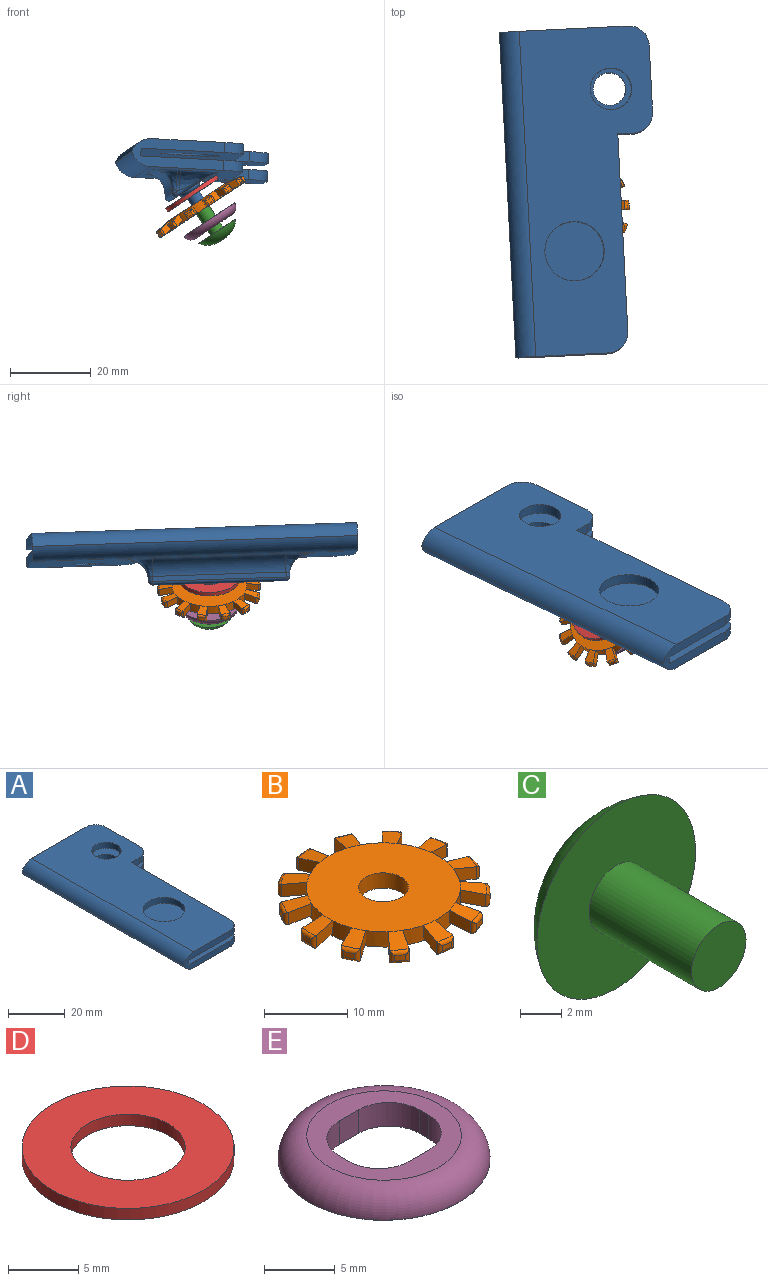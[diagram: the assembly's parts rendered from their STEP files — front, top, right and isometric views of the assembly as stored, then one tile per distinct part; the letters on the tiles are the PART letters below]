
ASSEMBLY  parts=5 mates=4
PART A: 50 faces, bbox 37.3x81.2x19.6 mm
  f0: plane 81.23x32.57mm, normal (0,0,-1), area 1317mm2, adj f1,f2,f3,f4,f5,f13,f14,f15
  f1: plane 31.76x6.93mm, normal (0,1,0), area 154.3mm2, adj f0,f9,f10,f11,f12,f13,f18,f19
  f2: plane 16.6x2.5mm, normal (1,0,0), area 41.5mm2, adj f0,f12,f13,f14
  f3: plane 3.89x2.5mm, normal (0,-1,0), area 9.7mm2, adj f0,f4,f12,f14
  f4: plane 49.06x2.5mm, normal (1,0,0), area 122.7mm2, adj f0,f3,f12,f15
  f5: plane 22.87x6.93mm, normal (0,-1,0), area 109.9mm2, adj f0,f9,f10,f11,f12,f15,f16,f19
  f6: plane 49.06x2.5mm, normal (1,0,0), area 122.7mm2, adj f7,f9,f11,f16
  f7: plane 3.89x2.5mm, normal (0,-1,0), area 9.7mm2, adj f6,f9,f11,f17
  f8: plane 16.6x2.5mm, normal (1,0,0), area 41.5mm2, adj f9,f11,f17,f18
  f9: plane 80.66x32mm, normal (0,0,1), area 1830.9mm2, adj f1,f5,f6,f7,f8,f16,f17,f18
  f10: plane 80.66x1.93mm, normal (1,0,0), area 155.7mm2, adj f1,f5,f11,f12
  f11: plane 80.66x34.5mm, normal (0,0,-1), area 2032.6mm2, adj f1,f5,f6,f7,f8,f10,f16,f17
  f12: plane 80.66x34.5mm, normal (0,0,1), area 2234.7mm2, adj f1,f2,f3,f4,f5,f10,f13,f14
  f13: cylinder r=5mm len=5mm, axis (0,0,-1), area 19.6mm2, adj f0,f1,f2,f12
  f14: cylinder r=5mm len=5mm, axis (0,0,-1), area 19.6mm2, adj f0,f2,f3,f12
  f15: cylinder r=5mm len=5mm, axis (0,0,-1), area 19.6mm2, adj f0,f4,f5,f12
  f16: cylinder r=5mm len=5mm, axis (0,0,-1), area 19.6mm2, adj f5,f6,f9,f11
  f17: cylinder r=5mm len=5mm, axis (0,0,-1), area 19.6mm2, adj f7,f8,f9,f11
  f18: cylinder r=5mm len=5mm, axis (0,0,-1), area 19.6mm2, adj f1,f8,f9,f11
  f19: cylinder r=5mm len=80.66mm, axis (0,1,0), area 507.7mm2, adj f1,f5,f9,f20
  f20: cylinder r=5mm len=80.66mm, axis (0,-1,0), area 507.7mm2, adj f0,f1,f5,f19
  f21: cylinder r=5.15mm len=10.3mm, axis (0,0,1), area 80.9mm2, adj f9,f11
  f22: cylinder r=4.04mm len=8.09mm, axis (0,0,-1), area 63.5mm2, adj f0,f12
  f23: cylinder r=7.36mm len=14.72mm, axis (0,0,1), area 115.6mm2, adj f9,f11
  f24: plane 33.07x7.22mm, normal (0.59,0,-0.81), area 269.9mm2, adj f28,f31,f34,f35,f43
  f25: plane 33.07x1.24mm, normal (-0.99,0,-0.12), area 41.2mm2, adj f29,f30,f34,f42
  f26: plane 0.75x0.51mm, normal (0,1,0), area 0.2mm2, adj f28,f29,f38
  f27: plane 0.75x0.51mm, normal (0,-1,0), area 0.2mm2, adj f30,f31,f39
  f28: cylinder r=0.97mm len=7.79mm, axis (-0.81,0,-0.59), area 9.1mm2, adj f24,f26,f32,f36
  f29: cylinder r=0.97mm len=1.35mm, axis (-0.12,0,0.99), area 1.3mm2, adj f25,f26,f32,f40
  f30: cylinder r=0.97mm len=1.35mm, axis (0.12,0,-0.99), area 1.3mm2, adj f25,f27,f33,f41
  f31: cylinder r=0.97mm len=7.79mm, axis (0.81,0,0.59), area 9.1mm2, adj f24,f27,f33,f37
  f32: sphere r=0.97mm, area 2.2mm2, adj f28,f29,f34
  f33: sphere r=0.97mm, area 2mm2, adj f30,f31,f34
  f34: cylinder r=0.97mm len=33.07mm, axis (0,-1,0), area 66.5mm2, adj f24,f25,f32,f33
  f35: cylinder r=5mm len=33.07mm, axis (0,1,0), area 104.9mm2, adj f0,f24,f36,f37
  f36: bspline ~10.06x5.97mm, area 51.8mm2, adj f0,f28,f35,f38
  f37: bspline ~10.06x5.97mm, area 51.8mm2, adj f0,f31,f35,f39
  f38: cylinder r=5mm len=5mm, axis (1,0,0), area 5.9mm2, adj f0,f26,f36,f40
  f39: cylinder r=5mm len=5mm, axis (-1,0,0), area 5.9mm2, adj f0,f27,f37,f41
  f40: bspline ~7.06x5.97mm, area 34mm2, adj f0,f29,f38,f42
  f41: bspline ~7.06x7mm, area 34mm2, adj f0,f30,f39,f42
  f42: cylinder r=5mm len=33.07mm, axis (0,1,0), area 239.5mm2, adj f0,f25,f40,f41
  f43: cylinder r=2.9mm len=5.8mm, axis (-0.59,0,0.81), area 0.3mm2, adj f24,f47
  f44: plane 4.01x3.23mm, normal (0.59,0,-0.81), area 3mm2, adj f45,f47
  f45: cylinder r=1.75mm len=8.71mm, axis (-0.59,0,0.81), area 90.6mm2, adj f44,f46
  f46: plane 3.5x2.82mm, normal (0.59,0,-0.81), area 5.3mm2, adj f45,f48
  f47: torus R=2.01mm, axis (0.59,0,-0.81), area 22.7mm2, adj f43,f44
  f48: cylinder r=1.18mm len=8.48mm, axis (0.59,0,-0.81), area 65mm2, adj f46,f49
  f49: plane 2.35x1.89mm, normal (0.59,0,-0.81), area 4.3mm2, adj f48
PART B: 121 faces, bbox 25.6x25.7x2.3 mm
  f0: cylinder r=9.24mm len=18.48mm, axis (0,0,-1), area 89.1mm2, adj f2,f3,f5,f7,f8,f14,f16,f17
  f1: cylinder r=3mm len=6mm, axis (0,0,-1), area 42.4mm2, adj f2,f3
  f2: plane 18.48x18.48mm, normal (0,0,1), area 239.9mm2, adj f0,f1,f4,f13,f22,f31,f40,f49
  f3: plane 18.48x18.48mm, normal (0,0,-1), area 239.9mm2, adj f0,f1
  f4: cone r=9.24mm half-angle=80deg, axis (0,0,-1), area 6.6mm2, adj f2,f7,f8,f9,f10,f11
  f5: cone r=12.79mm half-angle=80deg, axis (0,0,-1), area 6.2mm2, adj f0,f7,f8,f12
  f6: cylinder r=12.79mm len=1.39mm, axis (0,0,-1), area 1.1mm2, adj f9,f10,f11,f12
  f7: plane 2.98x2.33mm, normal (-0.98,-0.19,0), area 5.5mm2, adj f0,f4,f5,f10,f12
  f8: plane 3.03x2.33mm, normal (1,0,0), area 5.5mm2, adj f0,f4,f5,f11,f12
  f9: torus R=12.28mm, axis (0,0,1), area 1.4mm2, adj f4,f6,f10,f11
  f10: cylinder r=0.51mm len=1.79mm, axis (0,0,-1), area 1.2mm2, adj f4,f6,f7,f9,f12
  f11: cylinder r=0.51mm len=1.79mm, axis (0,0,-1), area 1.2mm2, adj f4,f6,f8,f9,f12
  f12: torus R=12.28mm, axis (0,0,1), area 1.8mm2, adj f5,f6,f7,f8,f10,f11
  f13: cone r=9.24mm half-angle=80deg, axis (0,0,-1), area 6.6mm2, adj f2,f16,f17,f18,f19,f20
  f14: cone r=12.79mm half-angle=80deg, axis (0,0,-1), area 6.2mm2, adj f0,f16,f17,f21
  f15: cylinder r=12.79mm len=1.17mm, axis (0,0,-1), area 1.1mm2, adj f18,f19,f20,f21
  f16: plane 2.37x2.33mm, normal (-0.78,-0.63,0), area 5.5mm2, adj f0,f13,f14,f19,f21
  f17: plane 2.69x2.33mm, normal (0.89,0.46,0), area 5.5mm2, adj f0,f13,f14,f20,f21
  f18: torus R=12.28mm, axis (0,0,1), area 1.4mm2, adj f13,f15,f19,f20
  f19: cylinder r=0.51mm len=1.79mm, axis (0,0,-1), area 1.2mm2, adj f13,f15,f16,f18,f21
  f20: cylinder r=0.51mm len=1.79mm, axis (0,0,-1), area 1.2mm2, adj f13,f15,f17,f18,f21
  f21: torus R=12.28mm, axis (0,0,1), area 1.8mm2, adj f14,f15,f16,f17,f19,f20
  f22: cone r=9.24mm half-angle=80deg, axis (0,0,-1), area 6.6mm2, adj f2,f25,f26,f27,f28,f29
  f23: cone r=12.79mm half-angle=80deg, axis (0,0,-1), area 6.2mm2, adj f0,f25,f26,f30
  f24: cylinder r=12.79mm len=1.4mm, axis (0,0,-1), area 1.1mm2, adj f27,f28,f29,f30
  f25: plane 3.03x2.33mm, normal (0.07,-1,0), area 5.5mm2, adj f0,f22,f23,f28,f30
  f26: plane 3.01x2.33mm, normal (0.12,0.99,0), area 5.5mm2, adj f0,f22,f23,f29,f30
  f27: torus R=12.28mm, axis (0,0,1), area 1.4mm2, adj f22,f24,f28,f29
  f28: cylinder r=0.51mm len=1.79mm, axis (0,0,-1), area 1.2mm2, adj f22,f24,f25,f27,f30
  f29: cylinder r=0.51mm len=1.79mm, axis (0,0,-1), area 1.2mm2, adj f22,f24,f26,f27,f30
  f30: torus R=12.28mm, axis (0,0,1), area 1.8mm2, adj f23,f24,f25,f26,f28,f29
  f31: cone r=9.24mm half-angle=80deg, axis (0,0,-1), area 6.6mm2, adj f2,f34,f35,f36,f37,f38
  f32: cone r=12.79mm half-angle=80deg, axis (0,0,-1), area 6.2mm2, adj f0,f34,f35,f39
  f33: cylinder r=12.79mm len=1.3mm, axis (0,0,-1), area 1.1mm2, adj f36,f37,f38,f39
  f34: plane 2.9x2.33mm, normal (-0.96,0.29,0), area 5.5mm2, adj f0,f31,f32,f37,f39
  f35: plane 2.69x2.33mm, normal (0.89,-0.46,0), area 5.5mm2, adj f0,f31,f32,f38,f39
  f36: torus R=12.28mm, axis (0,0,1), area 1.4mm2, adj f31,f33,f37,f38
  f37: cylinder r=0.51mm len=1.79mm, axis (0,0,-1), area 1.2mm2, adj f31,f33,f34,f36,f39
  f38: cylinder r=0.51mm len=1.79mm, axis (0,0,-1), area 1.2mm2, adj f31,f33,f35,f36,f39
  f39: torus R=12.28mm, axis (0,0,1), area 1.8mm2, adj f32,f33,f34,f35,f37,f38
  f40: cone r=9.24mm half-angle=80deg, axis (0,0,-1), area 6.6mm2, adj f2,f43,f44,f45,f46,f47
  f41: cone r=12.79mm half-angle=80deg, axis (0,0,-1), area 6.2mm2, adj f0,f43,f44,f48
  f42: cylinder r=12.79mm len=1.37mm, axis (0,0,-1), area 1.1mm2, adj f45,f46,f47,f48
  f43: plane 2.89x2.33mm, normal (-0.31,0.95,0), area 5.5mm2, adj f0,f40,f41,f46,f48
  f44: plane 3.01x2.33mm, normal (0.12,-0.99,0), area 5.5mm2, adj f0,f40,f41,f47,f48
  f45: torus R=12.28mm, axis (0,0,1), area 1.4mm2, adj f40,f42,f46,f47
  f46: cylinder r=0.51mm len=1.79mm, axis (0,0,-1), area 1.2mm2, adj f40,f42,f43,f45,f48
  f47: cylinder r=0.51mm len=1.79mm, axis (0,0,-1), area 1.2mm2, adj f40,f42,f44,f45,f48
  f48: torus R=12.28mm, axis (0,0,1), area 1.8mm2, adj f41,f42,f43,f44,f46,f47
  f49: cone r=9.24mm half-angle=80deg, axis (0,0,-1), area 6.6mm2, adj f2,f52,f53,f54,f55,f56
  f50: cone r=12.79mm half-angle=80deg, axis (0,0,-1), area 6.2mm2, adj f0,f52,f53,f57
  f51: cylinder r=12.79mm len=1.07mm, axis (0,0,-1), area 1.1mm2, adj f54,f55,f56,f57
  f52: plane 2.33x2.17mm, normal (-0.71,0.7,0), area 5.5mm2, adj f0,f49,f50,f55,f57
  f53: plane 2.5x2.33mm, normal (0.57,-0.82,0), area 5.5mm2, adj f0,f49,f50,f56,f57
  f54: torus R=12.28mm, axis (0,0,1), area 1.4mm2, adj f49,f51,f55,f56
  f55: cylinder r=0.51mm len=1.79mm, axis (0,0,-1), area 1.2mm2, adj f49,f51,f52,f54,f57
  f56: cylinder r=0.51mm len=1.79mm, axis (0,0,-1), area 1.2mm2, adj f49,f51,f53,f54,f57
  f57: torus R=12.28mm, axis (0,0,1), area 1.8mm2, adj f50,f51,f52,f53,f55,f56
  f58: cone r=9.24mm half-angle=80deg, axis (0,0,-1), area 6.6mm2, adj f2,f61,f62,f63,f64,f65
  f59: cone r=12.79mm half-angle=80deg, axis (0,0,-1), area 6.2mm2, adj f0,f61,f62,f66
  f60: cylinder r=12.79mm len=1.02mm, axis (0,0,-1), area 1.1mm2, adj f63,f64,f65,f66
  f61: plane 2.41x2.33mm, normal (0.61,0.79,0), area 5.5mm2, adj f0,f58,f59,f64,f66
  f62: plane 2.33x2.27mm, normal (-0.75,-0.66,0), area 5.5mm2, adj f0,f58,f59,f65,f66
  f63: torus R=12.28mm, axis (0,0,1), area 1.4mm2, adj f58,f60,f64,f65
  f64: cylinder r=0.51mm len=1.79mm, axis (0,0,-1), area 1.2mm2, adj f58,f60,f61,f63,f66
  f65: cylinder r=0.51mm len=1.79mm, axis (0,0,-1), area 1.2mm2, adj f58,f60,f62,f63,f66
  f66: torus R=12.28mm, axis (0,0,1), area 1.8mm2, adj f59,f60,f61,f62,f64,f65
  f67: cone r=9.24mm half-angle=80deg, axis (0,0,-1), area 6.6mm2, adj f2,f70,f71,f72,f73,f74
  f68: cone r=12.79mm half-angle=80deg, axis (0,0,-1), area 6.2mm2, adj f0,f70,f71,f75
  f69: cylinder r=12.79mm len=1.32mm, axis (0,0,-1), area 1.1mm2, adj f72,f73,f74,f75
  f70: plane 2.75x2.33mm, normal (0.91,0.42,0), area 5.5mm2, adj f0,f67,f68,f73,f75
  f71: plane 2.94x2.33mm, normal (-0.97,-0.24,0), area 5.5mm2, adj f0,f67,f68,f74,f75
  f72: torus R=12.28mm, axis (0,0,1), area 1.4mm2, adj f67,f69,f73,f74
  f73: cylinder r=0.51mm len=1.79mm, axis (0,0,-1), area 1.2mm2, adj f67,f69,f70,f72,f75
  f74: cylinder r=0.51mm len=1.79mm, axis (0,0,-1), area 1.2mm2, adj f67,f69,f71,f72,f75
  f75: torus R=12.28mm, axis (0,0,1), area 1.8mm2, adj f68,f69,f70,f71,f73,f74
  f76: cone r=9.24mm half-angle=80deg, axis (0,0,-1), area 6.6mm2, adj f2,f79,f80,f81,f82,f83
  f77: cone r=12.79mm half-angle=80deg, axis (0,0,-1), area 6.2mm2, adj f0,f79,f80,f84
  f78: cylinder r=12.79mm len=1.38mm, axis (0,0,-1), area 1.1mm2, adj f81,f82,f83,f84
  f79: plane 3.03x2.33mm, normal (1,-0.05,0), area 5.5mm2, adj f0,f76,f77,f82,f84
  f80: plane 2.94x2.33mm, normal (-0.97,0.24,0), area 5.5mm2, adj f0,f76,f77,f83,f84
  f81: torus R=12.28mm, axis (0,0,1), area 1.4mm2, adj f76,f78,f82,f83
  f82: cylinder r=0.51mm len=1.79mm, axis (0,0,-1), area 1.2mm2, adj f76,f78,f79,f81,f84
  f83: cylinder r=0.51mm len=1.79mm, axis (0,0,-1), area 1.2mm2, adj f76,f78,f80,f81,f84
  f84: torus R=12.28mm, axis (0,0,1), area 1.8mm2, adj f77,f78,f79,f80,f82,f83
  f85: cone r=9.24mm half-angle=80deg, axis (0,0,-1), area 6.6mm2, adj f2,f88,f89,f90,f91,f92
  f86: cone r=12.79mm half-angle=80deg, axis (0,0,-1), area 6.2mm2, adj f0,f88,f89,f93
  f87: cylinder r=12.79mm len=1.35mm, axis (0,0,-1), area 1.1mm2, adj f90,f91,f92,f93
  f88: plane 2.99x2.33mm, normal (0.17,0.99,0), area 5.5mm2, adj f0,f85,f86,f91,f93
  f89: plane 2.84x2.33mm, normal (-0.35,-0.94,0), area 5.5mm2, adj f0,f85,f86,f92,f93
  f90: torus R=12.28mm, axis (0,0,1), area 1.4mm2, adj f85,f87,f91,f92
  f91: cylinder r=0.51mm len=1.79mm, axis (0,0,-1), area 1.2mm2, adj f85,f87,f88,f90,f93
  f92: cylinder r=0.51mm len=1.79mm, axis (0,0,-1), area 1.2mm2, adj f85,f87,f89,f90,f93
  f93: torus R=12.28mm, axis (0,0,1), area 1.8mm2, adj f86,f87,f88,f89,f91,f92
  f94: cone r=9.24mm half-angle=80deg, axis (0,0,-1), area 6.6mm2, adj f2,f97,f98,f99,f100,f101
  f95: cone r=12.79mm half-angle=80deg, axis (0,0,-1), area 6.2mm2, adj f0,f97,f98,f102
  f96: cylinder r=12.79mm len=1.25mm, axis (0,0,-1), area 1.1mm2, adj f99,f100,f101,f102
  f97: plane 2.58x2.33mm, normal (0.53,-0.85,0), area 5.5mm2, adj f0,f94,f95,f100,f102
  f98: plane 2.84x2.33mm, normal (-0.35,0.94,0), area 5.5mm2, adj f0,f94,f95,f101,f102
  f99: torus R=12.28mm, axis (0,0,1), area 1.4mm2, adj f94,f96,f100,f101
  f100: cylinder r=0.51mm len=1.79mm, axis (0,0,-1), area 1.2mm2, adj f94,f96,f97,f99,f102
  f101: cylinder r=0.51mm len=1.79mm, axis (0,0,-1), area 1.2mm2, adj f94,f96,f98,f99,f102
  f102: torus R=12.28mm, axis (0,0,1), area 1.8mm2, adj f95,f96,f97,f98,f100,f101
  f103: cone r=9.24mm half-angle=80deg, axis (0,0,-1), area 6.6mm2, adj f2,f106,f107,f108,f109,f110
  f104: cone r=12.79mm half-angle=80deg, axis (0,0,-1), area 6.2mm2, adj f0,f106,f107,f111
  f105: cylinder r=12.79mm len=1.13mm, axis (0,0,-1), area 1.1mm2, adj f108,f109,f110,f111
  f106: plane 2.61x2.33mm, normal (0.86,-0.51,0), area 5.5mm2, adj f0,f103,f104,f109,f111
  f107: plane 2.33x2.27mm, normal (-0.75,0.66,0), area 5.5mm2, adj f0,f103,f104,f110,f111
  f108: torus R=12.28mm, axis (0,0,1), area 1.4mm2, adj f103,f105,f109,f110
  f109: cylinder r=0.51mm len=1.79mm, axis (0,0,-1), area 1.2mm2, adj f103,f105,f106,f108,f111
  f110: cylinder r=0.51mm len=1.79mm, axis (0,0,-1), area 1.2mm2, adj f103,f105,f107,f108,f111
  f111: torus R=12.28mm, axis (0,0,1), area 1.8mm2, adj f104,f105,f106,f107,f109,f110
  f112: cone r=9.24mm half-angle=80deg, axis (0,0,-1), area 6.6mm2, adj f2,f115,f116,f117,f118,f119
  f113: cone r=12.79mm half-angle=80deg, axis (0,0,-1), area 6.2mm2, adj f0,f115,f116,f120
  f114: cylinder r=12.79mm len=1.22mm, axis (0,0,-1), area 1.1mm2, adj f117,f118,f119,f120
  f115: plane 2.78x2.33mm, normal (-0.4,-0.92,0), area 5.5mm2, adj f0,f112,f113,f118,f120
  f116: plane 2.5x2.33mm, normal (0.57,0.82,0), area 5.5mm2, adj f0,f112,f113,f119,f120
  f117: torus R=12.28mm, axis (0,0,1), area 1.4mm2, adj f112,f114,f118,f119
  f118: cylinder r=0.51mm len=1.79mm, axis (0,0,-1), area 1.2mm2, adj f112,f114,f115,f117,f120
  f119: cylinder r=0.51mm len=1.79mm, axis (0,0,-1), area 1.2mm2, adj f112,f114,f116,f117,f120
  f120: torus R=12.28mm, axis (0,0,1), area 1.8mm2, adj f113,f114,f115,f116,f118,f119
PART C: 22 faces, bbox 10.8x9.4x10.8 mm
  f0: plane 10.83x10.83mm, normal (0,-1,0), area 81.3mm2, adj f2,f20
  f1: plane 2.29x2.29mm, normal (0,1,0), area 3.2mm2, adj f2,f3,f4,f5,f6,f7,f8,f9
  f2: torus R=1.14mm, axis (0,1,0), area 112.2mm2, adj f0,f1
  f3: plane 2.4x0.43mm, normal (-1,0,0), area 1mm2, adj f1,f4,f16,f19
  f4: plane 2.4x0.18mm, normal (0,0,1), area 0.4mm2, adj f1,f3,f5,f19
  f5: cylinder r=0.18mm len=2.4mm, axis (0,1,0), area 0.7mm2, adj f1,f4,f6,f19
  f6: plane 2.4x0.36mm, normal (-1,0,0), area 0.9mm2, adj f1,f5,f7,f19
  f7: plane 2.4x0.42mm, normal (0,0,1), area 1mm2, adj f1,f6,f8,f19
  f8: plane 2.4x0.36mm, normal (1,0,0), area 0.9mm2, adj f1,f7,f9,f19
  f9: cylinder r=0.18mm len=2.4mm, axis (0,1,0), area 0.7mm2, adj f1,f8,f10,f19
  f10: plane 2.4x0.22mm, normal (0,0,1), area 0.5mm2, adj f1,f9,f11,f19
  f11: plane 2.4x0.43mm, normal (1,0,0), area 1mm2, adj f1,f10,f12,f19
  f12: plane 2.4x0.22mm, normal (0,0,-1), area 0.5mm2, adj f1,f11,f13,f19
  f13: cylinder r=0.18mm len=2.4mm, axis (0,1,0), area 0.7mm2, adj f1,f12,f14,f19
  f14: plane 2.4x0.25mm, normal (1,0,0), area 0.6mm2, adj f1,f13,f15,f19
  f15: plane 2.4x0.42mm, normal (0,0,-1), area 1mm2, adj f1,f14,f17,f19
  f16: plane 2.4x0.18mm, normal (0,0,-1), area 0.4mm2, adj f1,f3,f18,f19
  f17: plane 2.4x0.25mm, normal (-1,0,0), area 0.6mm2, adj f1,f15,f18,f19
  f18: cylinder r=0.18mm len=2.4mm, axis (0,1,0), area 0.7mm2, adj f1,f16,f17,f19
  f19: plane 1.42x1.19mm, normal (0,1,0), area 1mm2, adj f3,f4,f5,f6,f7,f8,f9,f10
  f20: cylinder r=1.86mm len=7mm, axis (0,1,0), area 81.6mm2, adj f0,f21
  f21: plane 3.71x3.71mm, normal (0,-1,0), area 10.8mm2, adj f20
PART D: 4 faces, bbox 15.1x15.1x1 mm
  f0: cylinder r=4.06mm len=8.12mm, axis (0,0,-1), area 25.5mm2, adj f2,f3
  f1: cylinder r=7.53mm len=15.06mm, axis (0,0,-1), area 47.3mm2, adj f2,f3
  f2: plane 15.06x15.06mm, normal (0,0,1), area 126.3mm2, adj f0,f1
  f3: plane 15.06x15.06mm, normal (0,0,-1), area 126.3mm2, adj f0,f1
PART E: 12 faces, bbox 16.2x16.2x2 mm
  f0: cylinder r=3.04mm len=3.04mm, axis (0,0,-1), area 9.7mm2, adj f1,f7,f9,f10
  f1: plane 2.04x0.92mm, normal (1,0,0), area 1.9mm2, adj f0,f2,f9,f10
  f2: cylinder r=3.04mm len=3.04mm, axis (0,0,-1), area 9.7mm2, adj f1,f3,f9,f10
  f3: plane 2.04x1.92mm, normal (0,-1,0), area 3.9mm2, adj f2,f4,f9,f10
  f4: cylinder r=3.04mm len=3.04mm, axis (0,0,-1), area 9.7mm2, adj f3,f5,f9,f10
  f5: plane 2.04x0.92mm, normal (-1,0,0), area 1.9mm2, adj f4,f6,f9,f10
  f6: cylinder r=3.04mm len=3.04mm, axis (0,0,-1), area 9.7mm2, adj f5,f7,f9,f10
  f7: plane 2.04x1.92mm, normal (0,1,0), area 3.9mm2, adj f0,f6,f9,f10
  f8: cylinder r=7.5mm len=15mm, axis (0,0,-1), area 0.6mm2, adj f10,f11
  f9: plane 10.94x10.94mm, normal (0,0,1), area 46mm2, adj f0,f1,f2,f3,f4,f5,f6,f7
  f10: plane 15x15mm, normal (0,0,-1), area 128.7mm2, adj f0,f1,f2,f3,f4,f5,f6,f7
  f11: torus R=5.47mm, axis (0,0,1), area 135.4mm2, adj f8,f9
PLACE A rot(axis=(-0.43,0.65,0.62),4.6deg) t=(31.25,6.69,8.11)mm
PLACE B rot(axis=(-0.24,-0.54,0.81),58deg) t=(-0.08,20.26,0.58)mm
PLACE C rot(axis=(-0.92,-0.3,-0.25),95.7deg) t=(4.77,20.26,-6.87)mm
PLACE D rot(axis=(0,-1,0),33.4deg) t=(-2.42,20.26,4.13)mm
PLACE E rot(axis=(-0.96,0,-0.29),180deg) t=(1.53,20.26,-1.94)mm
MATE revolute B.f1 <-> A.f47  axis (0.55,0,-0.84) through (-0.7,20.26,1.52)mm
MATE revolute D.f0 <-> A.f47  axis (0.55,0,-0.84) through (-2.97,20.26,4.96)mm
MATE revolute E.f8 <-> A.f48  axis (-0.55,0,0.84) through (1.53,20.26,-1.94)mm
MATE fastened C.f20 <-> A.f48  axis (0.55,0,-0.84) through (1.53,20.26,-1.94)mm
